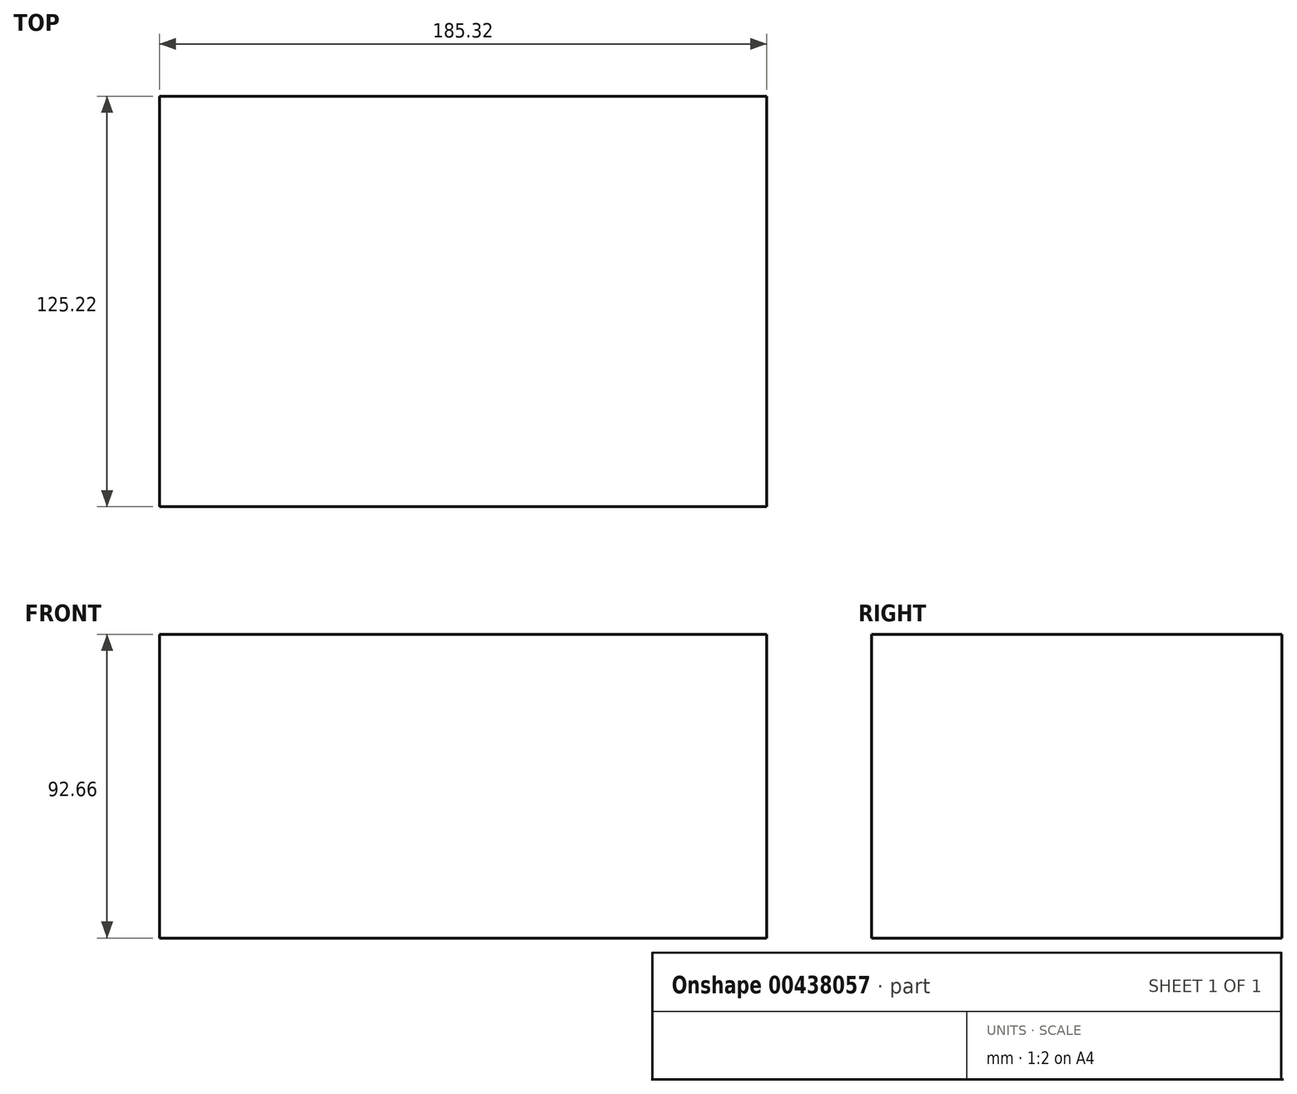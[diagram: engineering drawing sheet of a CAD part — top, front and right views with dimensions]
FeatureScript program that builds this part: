
annotation { "Feature Type Name" : "Feature", "Feature Type Description" : "" }
export const myFeature = defineFeature(function(context is Context, id is Id, definition is map)
    precondition{}
    {
        {
            var Q0;
            Q0=qCreatedBy(makeId("Front.planeOp"),FACE);
            var sketch = newSketch(context, id + "F0", { "sketchPlane" : qUnion([Q0])});
            skLineSegment(sketch, "E0.bottom", {"start": v(-92.66, 46.48) * mm, "end": v(92.66, 46.48) * mm});
            skLineSegment(sketch, "E0.top", {"start": v(-92.66, -46.18) * mm, "end": v(92.66, -46.18) * mm});
            skLineSegment(sketch, "E0.left", {"start": v(-92.66, 46.48) * mm, "end": v(-92.66, -46.18) * mm});
            skLineSegment(sketch, "E0.right", {"start": v(92.66, 46.48) * mm, "end": v(92.66, -46.18) * mm});
            skSolve(sketch);
        }
        {
            var Q0;
            Q0 = qSketchRegion(id + "F0", true);
            extrude(context, id + "F1", {"entities" : qUnion([Q0]), "depth" : 125.22 * mm});
        }
    });
